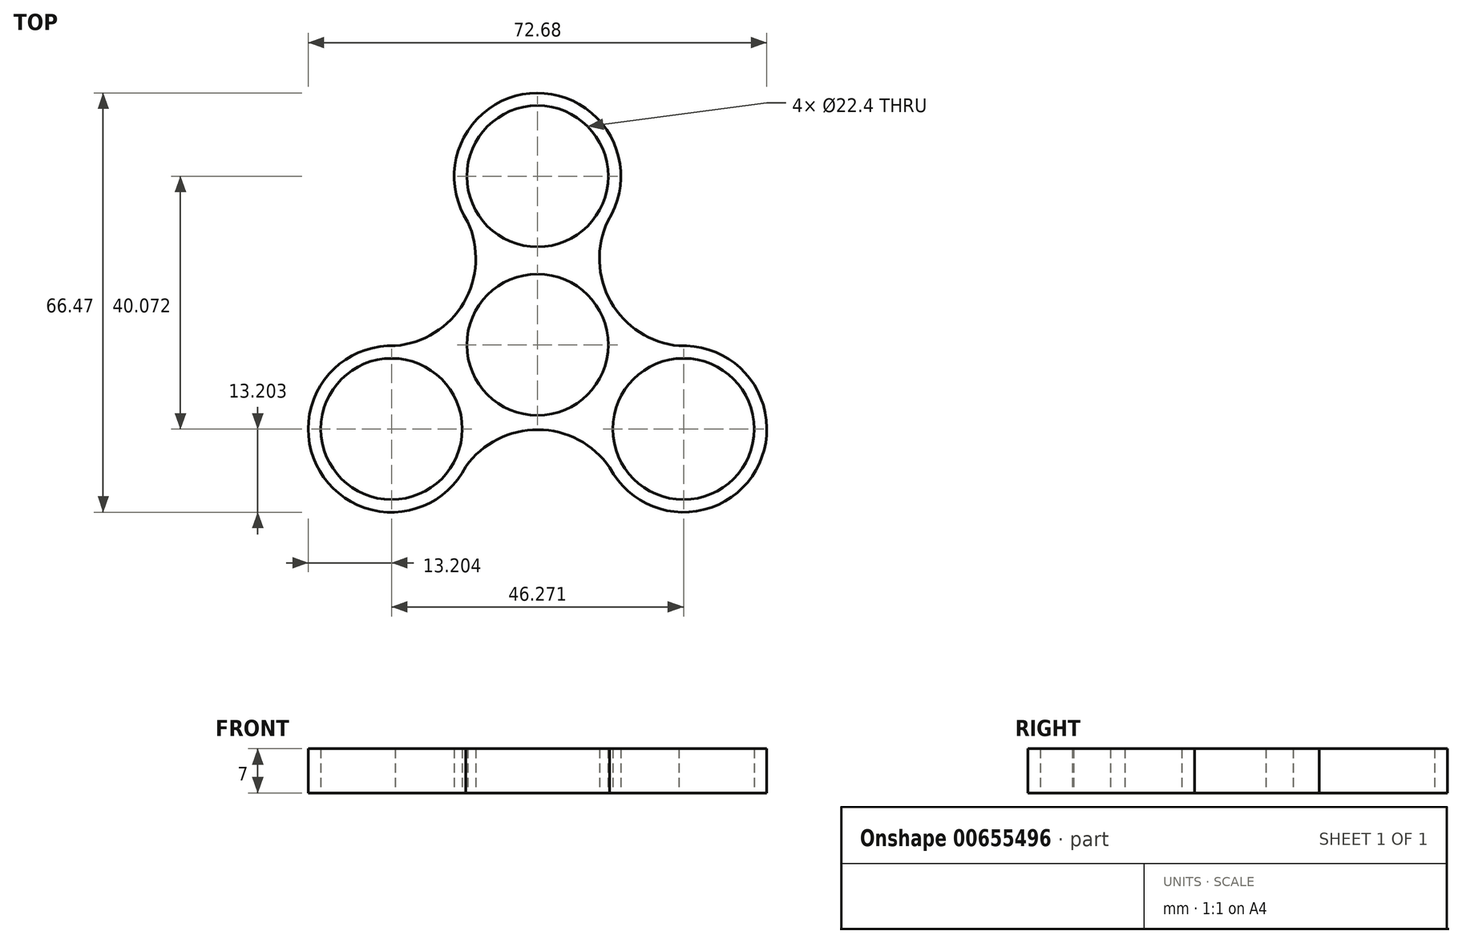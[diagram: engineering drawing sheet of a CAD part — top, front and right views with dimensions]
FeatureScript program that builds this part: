
annotation { "Feature Type Name" : "Feature", "Feature Type Description" : "" }
export const myFeature = defineFeature(function(context is Context, id is Id, definition is map)
    precondition{}
    {
        {
            var Q0;
            Q0=qCreatedBy(makeId("Top.planeOp"),FACE);
            var sketch = newSketch(context, id + "F0", { "sketchPlane" : qUnion([Q0])});
            skCircle(sketch, "E0", {"center": v(0, 0) * mm, "radius": 11.2 * mm});
            skArc(sketch, "E1", {"start": v(11.14, 19.64) * mm, "mid": v(-0.09, 39.91) * mm, "end": v(-11.04, 19.49) * mm});
            skCircle(sketch, "E2", {"center": v(0, 26.71) * mm, "radius": 11.2 * mm});
            skCircle(sketch, "E3.1.0", {"center": v(-23.14, -13.36) * mm, "radius": 11.2 * mm});
            skArc(sketch, "E3.1.1", {"start": v(-22.58, -0.17) * mm, "mid": v(-34.52, -20.04) * mm, "end": v(-11.35, -19.3) * mm});
            skCircle(sketch, "E3.2.0", {"center": v(23.14, -13.36) * mm, "radius": 11.2 * mm});
            skArc(sketch, "E3.2.1", {"start": v(11.44, -19.47) * mm, "mid": v(34.61, -19.88) * mm, "end": v(22.4, -0.18) * mm});
            skArc(sketch, "E4", {"start": v(11.14, 19.64) * mm, "mid": v(11.62, 6.8) * mm, "end": v(22.4, -0.18) * mm});
            skArc(sketch, "E5.1.0", {"start": v(-22.58, -0.17) * mm, "mid": v(-11.7, 6.66) * mm, "end": v(-11.04, 19.49) * mm});
            skArc(sketch, "E5.2.0", {"start": v(11.44, -19.47) * mm, "mid": v(0.08, -13.47) * mm, "end": v(-11.35, -19.3) * mm});
            skSolve(sketch);
        }
        {
            var Q0;
            Q0=makeQuery(id+"F0.imprint","IMPRINT",FACE,{"disambiguationData":[TD([[makeQuery(id+"F0.imprint","IMPRINT",EDGE,{"derivedFrom":sQuery(id+"F0.wireOp",EDGE,"E0")}),-1.0]])]});
            var Q1;
            {var subQ0=sQuery(id+"F0.wireOp",EDGE,"LvyE8la5-3Vhn-HZ7e-L34a-owlSgBMoA8po");Q1=makeQuery(id+"F0.imprint","IMPRINT",FACE,{"disambiguationData":[TD([[makeQuery(id+"F0.imprint","IMPRINT",EDGE,{"derivedFrom":subQ0}),1.0]])]});}
            var Q2;
            {var subQ0=sQuery(id+"F0.wireOp",EDGE,"08060f57-af42-442d-bbbe-c0b19dcd397a.2.0");Q2=makeQuery(id+"F0.imprint","IMPRINT",FACE,{"disambiguationData":[TD([[makeQuery(id+"F0.imprint","IMPRINT",EDGE,{"derivedFrom":subQ0}),1.0]])]});}
            var Q3;
            {var subQ0=sQuery(id+"F0.wireOp",EDGE,"08060f57-af42-442d-bbbe-c0b19dcd397a.1.0");Q3=makeQuery(id+"F0.imprint","IMPRINT",FACE,{"disambiguationData":[TD([[makeQuery(id+"F0.imprint","IMPRINT",EDGE,{"derivedFrom":subQ0}),1.0]])]});}
            extrude(context, id + "F1", {"entities" : qUnion([Q0, Q1, Q2, Q3]), "depth" : 7 * mm, "offsetDistance" : 25 * mm});
        }
        {
            var Q0;
            Q0=makeQuery(id+"F1.opExtrude","CAP_EDGE",EDGE,{"disambiguationData":[OSD([sQuery(id+"F0.wireOp",EDGE,"E3.1.1")])],"isStart":false});
            var Q1;
            Q1=makeQuery(id+"F1.opExtrude","CAP_EDGE",EDGE,{"disambiguationData":[OSD([sQuery(id+"F0.wireOp",EDGE,"E5.1.0")])],"isStart":false});
            var Q2;
            Q2=makeQuery(id+"F1.opExtrude","CAP_EDGE",EDGE,{"disambiguationData":[OSD([sQuery(id+"F0.wireOp",EDGE,"E3.2.1")])],"isStart":false});
            var Q3;
            Q3=makeQuery(id+"F1.opExtrude","CAP_EDGE",EDGE,{"disambiguationData":[OSD([sQuery(id+"F0.wireOp",EDGE,"E3.2.1")])],"isStart":true});
            var Q4;
            Q4=makeQuery(id+"F1.opExtrude","CAP_EDGE",EDGE,{"disambiguationData":[OSD([sQuery(id+"F0.wireOp",EDGE,"E5.2.0")])],"isStart":true});
            var Q5;
            Q5=makeQuery(id+"F1.opExtrude","CAP_EDGE",EDGE,{"disambiguationData":[OSD([sQuery(id+"F0.wireOp",EDGE,"E3.1.1")])],"isStart":true});
            var Q6;
            Q6=makeQuery(id+"F1.opExtrude","CAP_EDGE",EDGE,{"disambiguationData":[OSD([sQuery(id+"F0.wireOp",EDGE,"E1")])],"isStart":false});
            var Q7;
            Q7=makeQuery(id+"F1.opExtrude","CAP_EDGE",EDGE,{"disambiguationData":[OSD([sQuery(id+"F0.wireOp",EDGE,"E1")])],"isStart":true});
            var Q8;
            Q8=makeQuery(id+"F1.opExtrude","CAP_EDGE",EDGE,{"disambiguationData":[OSD([sQuery(id+"F0.wireOp",EDGE,"E4")])],"isStart":true});
            var Q9;
            Q9=makeQuery(id+"F1.opExtrude","CAP_EDGE",EDGE,{"disambiguationData":[OSD([sQuery(id+"F0.wireOp",EDGE,"E5.1.0")])],"isStart":true});
            var Q10;
            Q10=makeQuery(id+"F1.opExtrude","CAP_EDGE",EDGE,{"disambiguationData":[OSD([sQuery(id+"F0.wireOp",EDGE,"E5.2.0")])],"isStart":false});
            var Q11;
            Q11=makeQuery(id+"F1.opExtrude","CAP_EDGE",EDGE,{"disambiguationData":[OSD([sQuery(id+"F0.wireOp",EDGE,"E4")])],"isStart":false});
            var Q12;
            Q12=makeQuery(id+"F1.opExtrude","CAP_EDGE",EDGE,{"disambiguationData":[OSD([sQuery(id+"F0.wireOp",EDGE,"08060f57-af42-442d-bbbe-c0b19dcd397a.1.0")])],"isStart":true});
            var Q13;
            Q13=makeQuery(id+"F1.opExtrude","CAP_EDGE",EDGE,{"disambiguationData":[OSD([sQuery(id+"F0.wireOp",EDGE,"08060f57-af42-442d-bbbe-c0b19dcd397a.1.1")])],"isStart":true});
            var Q14;
            Q14=makeQuery(id+"F1.opExtrude","CAP_EDGE",EDGE,{"disambiguationData":[OSD([sQuery(id+"F0.wireOp",EDGE,"TDcdATS3-oKia-FStB-4fkk-9tCUpAREQDiA")])],"isStart":true});
            var Q15;
            Q15=makeQuery(id+"F1.opExtrude","CAP_EDGE",EDGE,{"disambiguationData":[OSD([sQuery(id+"F0.wireOp",EDGE,"LvyE8la5-3Vhn-HZ7e-L34a-owlSgBMoA8po")])],"isStart":true});
            var Q16;
            Q16=makeQuery(id+"F1.opExtrude","CAP_EDGE",EDGE,{"disambiguationData":[OSD([sQuery(id+"F0.wireOp",EDGE,"08060f57-af42-442d-bbbe-c0b19dcd397a.2.0")])],"isStart":true});
            var Q17;
            Q17=makeQuery(id+"F1.opExtrude","CAP_EDGE",EDGE,{"disambiguationData":[OSD([sQuery(id+"F0.wireOp",EDGE,"08060f57-af42-442d-bbbe-c0b19dcd397a.2.1")])],"isStart":true});
            var Q18;
            Q18=makeQuery(id+"F1.opExtrude","CAP_EDGE",EDGE,{"disambiguationData":[OSD([sQuery(id+"F0.wireOp",EDGE,"TDcdATS3-oKia-FStB-4fkk-9tCUpAREQDiA")])],"isStart":false});
            var Q19;
            Q19=makeQuery(id+"F1.opExtrude","CAP_EDGE",EDGE,{"disambiguationData":[OSD([sQuery(id+"F0.wireOp",EDGE,"LvyE8la5-3Vhn-HZ7e-L34a-owlSgBMoA8po")])],"isStart":false});
            var Q20;
            Q20=makeQuery(id+"F1.opExtrude","CAP_EDGE",EDGE,{"disambiguationData":[OSD([sQuery(id+"F0.wireOp",EDGE,"08060f57-af42-442d-bbbe-c0b19dcd397a.1.1")])],"isStart":false});
            var Q21;
            Q21=makeQuery(id+"F1.opExtrude","CAP_EDGE",EDGE,{"disambiguationData":[OSD([sQuery(id+"F0.wireOp",EDGE,"08060f57-af42-442d-bbbe-c0b19dcd397a.1.0")])],"isStart":false});
            var Q22;
            Q22=makeQuery(id+"F1.opExtrude","CAP_EDGE",EDGE,{"disambiguationData":[OSD([sQuery(id+"F0.wireOp",EDGE,"08060f57-af42-442d-bbbe-c0b19dcd397a.2.1")])],"isStart":false});
            var Q23;
            Q23=makeQuery(id+"F1.opExtrude","CAP_EDGE",EDGE,{"disambiguationData":[OSD([sQuery(id+"F0.wireOp",EDGE,"08060f57-af42-442d-bbbe-c0b19dcd397a.2.0")])],"isStart":false});
            fillet(context, id + "F2", {"entities" : qUnion([Q0, Q1, Q2, Q3, Q4, Q5, Q6, Q7, Q8, Q9, Q10, Q11, Q12, Q13, Q14, Q15, Q16, Q17, Q18, Q19, Q20, Q21, Q22, Q23]), "radius" : 1.5 * mm, "tangentPropagation" : true, "allowEdgeOverflow" : false});
        }
        {
            var Q0;
            Q0 = qSketchRegion(id + "F0", true);
            extrude(context, id + "F3", {"entities" : qUnion([Q0]), "operationType" : NewBodyOperationType.ADD, "depth" : 7 * mm, "offsetDistance" : 25 * mm});
        }
    });
